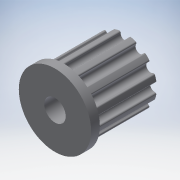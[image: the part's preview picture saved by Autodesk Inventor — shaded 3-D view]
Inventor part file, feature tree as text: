
AUTODESK INVENTOR PART (.ipt)
format: ipt  version: 2018.2 (Build 222227000, 227)  size: 185,344 bytes
history: native  units: mm
features: extrude x3, sketch x3, pattern_circular x1
ambient origin geometry x8: Origin, YZ Plane, XZ Plane, XY Plane, X Axis, Y Axis, Z Axis, Center Point
bodies: Solid1 (feature_tree)
feature tree (7):
  extrude  "Extrusion1"  Depth=0.5mm
  extrude  "Extrusion2"  Depth=7.0mm TaperAngle=0.0deg
  pattern_circular  "Circular Pattern1"  [2 undecoded]
  extrude  "Extrusion3"  TaperAngle=0.0deg  [1 undecoded]
  sketch  "Sketch1"  dims[d8=0.0mm d9=0.5mm]
  sketch  "Sketch2"  dims[d10=0.15mm d12=7.0mm d13=0.0mm]
  sketch  "Sketch3"  dims[d15=360.0deg d18=2.45mm d20=0.0mm]
note: 3 required parameter values undecoded (feature->parameter linkage not recoverable at this tier; creation-order binding heuristic only, values carry confidence <= 0.55)
